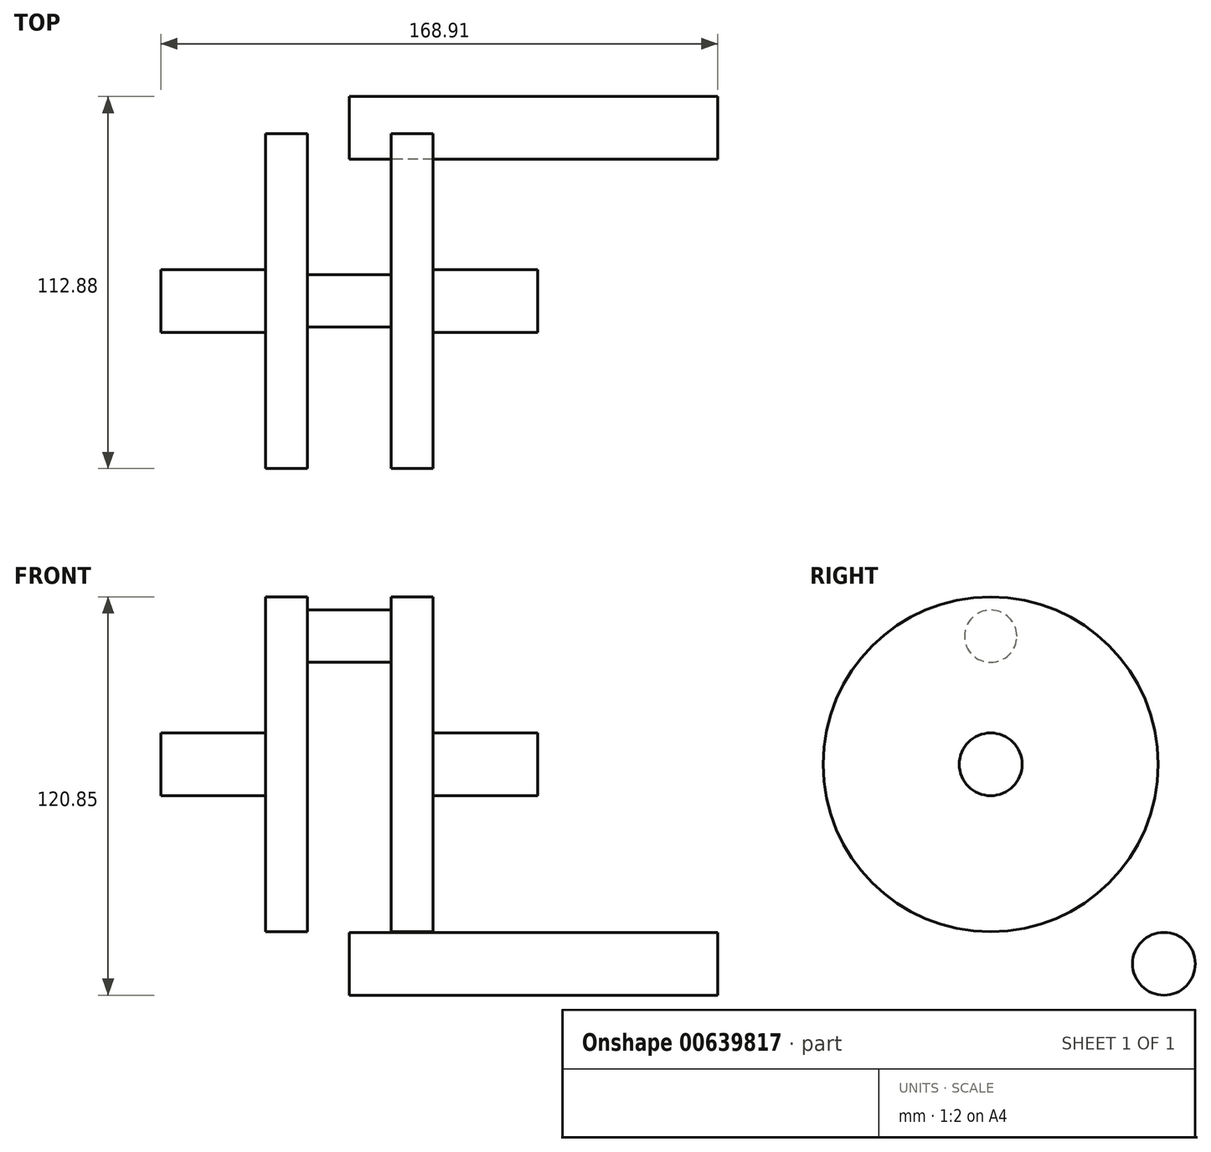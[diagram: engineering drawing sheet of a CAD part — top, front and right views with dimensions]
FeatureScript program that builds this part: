
annotation { "Feature Type Name" : "Feature", "Feature Type Description" : "" }
export const myFeature = defineFeature(function(context is Context, id is Id, definition is map)
    precondition{}
    {
        {
            var Q0;
            Q0=qCreatedBy(makeId("Front.planeOp"),FACE);
            var sketch = newSketch(context, id + "F0", { "sketchPlane" : qUnion([Q0])});
            skLineSegment(sketch, "E0.bottom", {"start": v(-25.4, 0) * mm, "end": v(-57.15, 0) * mm});
            skLineSegment(sketch, "E0.top", {"start": v(-25.4, 9.53) * mm, "end": v(-57.15, 9.53) * mm});
            skLineSegment(sketch, "E0.left", {"start": v(-25.4, 0) * mm, "end": v(-25.4, 9.53) * mm});
            skLineSegment(sketch, "E0.right", {"start": v(-57.15, 0) * mm, "end": v(-57.15, 9.53) * mm});
            skPoint(sketch, "E0.middle", {"position": v(-41.28, 4.76) * mm});
            skLineSegment(sketch, "E1.bottom", {"start": v(-25.4, 0) * mm, "end": v(-12.7, 0) * mm});
            skLineSegment(sketch, "E1.top", {"start": v(-25.4, 50.8) * mm, "end": v(-12.7, 50.8) * mm});
            skLineSegment(sketch, "E1.left", {"start": v(-25.4, 0) * mm, "end": v(-25.4, 50.8) * mm});
            skLineSegment(sketch, "E1.right", {"start": v(-12.7, 0) * mm, "end": v(-12.7, 50.8) * mm});
            skPoint(sketch, "E1.middle", {"position": v(-19.05, 25.4) * mm});
            skLineSegment(sketch, "E2.bottom", {"start": v(57.15, 0) * mm, "end": v(25.4, 0) * mm});
            skLineSegment(sketch, "E2.top", {"start": v(57.15, 9.52) * mm, "end": v(25.4, 9.52) * mm});
            skLineSegment(sketch, "E2.left", {"start": v(57.15, 0) * mm, "end": v(57.15, 9.53) * mm});
            skLineSegment(sketch, "E2.right", {"start": v(25.4, 0) * mm, "end": v(25.4, 9.52) * mm});
            skPoint(sketch, "E2.middle", {"position": v(41.28, 4.76) * mm});
            skLineSegment(sketch, "E3.bottom", {"start": v(25.4, 0) * mm, "end": v(12.7, 0) * mm});
            skLineSegment(sketch, "E3.top", {"start": v(25.4, 50.8) * mm, "end": v(12.7, 50.8) * mm});
            skLineSegment(sketch, "E3.left", {"start": v(25.4, 0) * mm, "end": v(25.4, 50.8) * mm});
            skLineSegment(sketch, "E3.right", {"start": v(12.7, 0) * mm, "end": v(12.7, 50.8) * mm});
            skPoint(sketch, "E3.middle", {"position": v(19.05, 25.4) * mm});
            skLineSegment(sketch, "E4.bottom", {"start": v(-12.7, 46.83) * mm, "end": v(12.7, 46.83) * mm});
            skLineSegment(sketch, "E4.top", {"start": v(-12.7, 38.9) * mm, "end": v(12.7, 38.9) * mm});
            skLineSegment(sketch, "E4.left", {"start": v(-12.7, 46.83) * mm, "end": v(-12.7, 38.9) * mm});
            skLineSegment(sketch, "E4.right", {"start": v(12.7, 46.83) * mm, "end": v(12.7, 38.9) * mm});
            skPoint(sketch, "E4.middle", {"position": v(0, 42.86) * mm});
            skSolve(sketch);
        }
        {
            var Q0;
            {var subQ0=sQuery(id+"F0.wireOp",EDGE,"E0.bottom");Q0=makeQuery(id+"F0.imprint","IMPRINT",FACE,{"disambiguationData":[TD([[makeQuery(id+"F0.imprint","IMPRINT",EDGE,{"derivedFrom":subQ0}),-1.0]])]});}
            var Q1;
            {var subQ3=sQuery(id+"F0.wireOp",EDGE,"E1.bottom");Q1=makeQuery(id+"F0.imprint","IMPRINT",FACE,{"disambiguationData":[TD([[makeQuery(id+"F0.imprint","IMPRINT",EDGE,{"derivedFrom":subQ3}),1.0]])]});}
            var Q2;
            {var subQ3=sQuery(id+"F0.wireOp",EDGE,"E3.bottom");Q2=makeQuery(id+"F0.imprint","IMPRINT",FACE,{"disambiguationData":[TD([[makeQuery(id+"F0.imprint","IMPRINT",EDGE,{"derivedFrom":subQ3}),-1.0]])]});}
            var Q3;
            {var subQ0=sQuery(id+"F0.wireOp",EDGE,"E2.bottom");Q3=makeQuery(id+"F0.imprint","IMPRINT",FACE,{"disambiguationData":[TD([[makeQuery(id+"F0.imprint","IMPRINT",EDGE,{"derivedFrom":subQ0}),-1.0]])]});}
            var Q4;
            Q4=sQuery(id+"F0.wireOp",EDGE,"E0.bottom");
            revolve(context, id + "F1", {"entities" : qUnion([Q0, Q1, Q2, Q3]), "axis" : qUnion([Q4]), "revolveType" : RevolveType.FULL});
        }
        {
            var Q0;
            Q0=qCreatedBy(makeId("Front.planeOp"),FACE);
            var sketch = newSketch(context, id + "F2", { "sketchPlane" : qUnion([Q0])});
            skLineSegment(sketch, "E5.bottom", {"start": v(-12.7, 38.9) * mm, "end": v(12.7, 38.9) * mm});
            skLineSegment(sketch, "E5.top", {"start": v(-12.7, 46.83) * mm, "end": v(12.7, 46.83) * mm});
            skLineSegment(sketch, "E5.left", {"start": v(-12.7, 38.9) * mm, "end": v(-12.7, 46.83) * mm});
            skLineSegment(sketch, "E5.right", {"start": v(12.7, 38.9) * mm, "end": v(12.7, 46.83) * mm});
            skPoint(sketch, "E5.middle", {"position": v(0, 42.86) * mm});
            skSolve(sketch);
        }
        {
            var Q0;
            Q0=makeQuery(id+"F2.imprint","IMPRINT",FACE,{"disambiguationData":[TD([[makeQuery(id+"F2.imprint","IMPRINT",EDGE,{"derivedFrom":sQuery(id+"F2.wireOp",EDGE,"E5.bottom")}),1.0]])]});
            var Q1;
            Q1=sQuery(id+"F2.wireOp",EDGE,"E5.bottom");
            revolve(context, id + "F3", {"entities" : qUnion([Q0]), "axis" : qUnion([Q1]), "revolveType" : RevolveType.FULL});
        }
        {
            var Q0;
            Q0=qCreatedBy(makeId("Right.planeOp"),FACE);
            var sketch = newSketch(context, id + "F4", { "sketchPlane" : qUnion([Q0])});
            skCircle(sketch, "E6", {"center": v(52.55, -60.52) * mm, "radius": 9.53 * mm});
            skSolve(sketch);
        }
        {
            var Q0;
            Q0=makeQuery(id+"F4.imprint","IMPRINT",FACE,{"disambiguationData":[TD([[makeQuery(id+"F4.imprint","IMPRINT",EDGE,{"derivedFrom":sQuery(id+"F4.wireOp",EDGE,"E6")}),1.0]])]});
            extrude(context, id + "F5", {"entities" : qUnion([Q0]), "depth" : 111.76 * mm, "offsetDistance" : 25.4 * mm});
        }
    });
